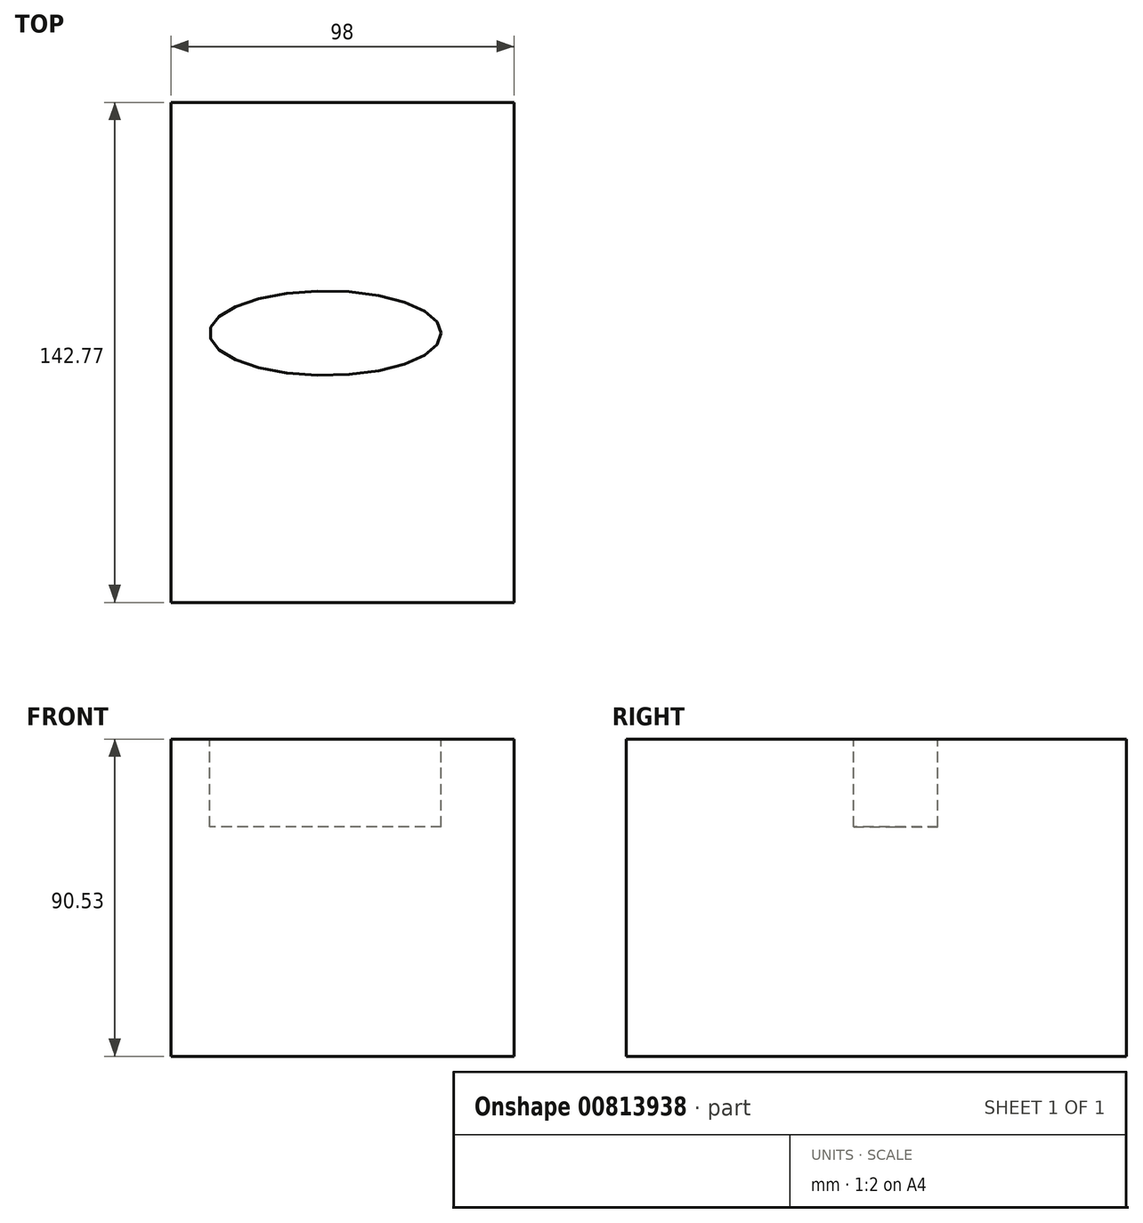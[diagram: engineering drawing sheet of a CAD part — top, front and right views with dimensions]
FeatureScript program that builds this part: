
annotation { "Feature Type Name" : "Feature", "Feature Type Description" : "" }
export const myFeature = defineFeature(function(context is Context, id is Id, definition is map)
    precondition{}
    {
        {
            var Q0;
            Q0=qCreatedBy(makeId("Top.planeOp"),FACE);
            var sketch = newSketch(context, id + "F0", { "sketchPlane" : qUnion([Q0])});
            skLineSegment(sketch, "E0.bottom", {"start": v(-59.05, -89.04) * mm, "end": v(38.95, -89.04) * mm});
            skLineSegment(sketch, "E0.top", {"start": v(-59.05, 53.73) * mm, "end": v(38.95, 53.73) * mm});
            skLineSegment(sketch, "E0.left", {"start": v(-59.05, -89.04) * mm, "end": v(-59.05, 53.73) * mm});
            skLineSegment(sketch, "E0.right", {"start": v(38.95, -89.04) * mm, "end": v(38.95, 53.73) * mm});
            skSolve(sketch);
        }
        {
            var Q0;
            Q0=makeQuery(id+"F0.imprint","IMPRINT",FACE,{"disambiguationData":[TD([[makeQuery(id+"F0.imprint","IMPRINT",EDGE,{"derivedFrom":sQuery(id+"F0.wireOp",EDGE,"E0.bottom")}),1.0]])]});
            extrude(context, id + "F1", {"entities" : qUnion([Q0]), "depth" : 90.53 * mm, "offsetDistance" : 25 * mm});
        }
        {
            var Q0;
            Q0=makeQuery(id+"F1.opExtrude","CAP_FACE",FACE,{"disambiguationData":[OSD([sQuery(id+"F0.wireOp",EDGE,"E0.bottom"),sQuery(id+"F0.wireOp",EDGE,"E0.top"),sQuery(id+"F0.wireOp",EDGE,"E0.left"),sQuery(id+"F0.wireOp",EDGE,"E0.right")])],"isStart":false});
            var sketch = newSketch(context, id + "F2", { "sketchPlane" : qUnion([Q0])});
            skEllipse(sketch, "E1", {"center": v(-14.92, -12.16) * mm, "majorRadius": 12.05 * mm, "minorRadius": 33.07 * mm, "majorAxis": v(0, -1)});
            skSolve(sketch);
        }
        {
            var Q0;
            Q0=makeQuery(id+"F2.imprint","IMPRINT",FACE,{"disambiguationData":[TD([[makeQuery(id+"F2.imprint","IMPRINT",EDGE,{"derivedFrom":sQuery(id+"F2.wireOp",EDGE,"E1")}),1.0]])]});
            extrude(context, id + "F3", {"entities" : qUnion([Q0]), "operationType" : NewBodyOperationType.REMOVE, "oppositeDirection" : true, "depth" : 25 * mm, "offsetDistance" : 25 * mm});
        }
    });
